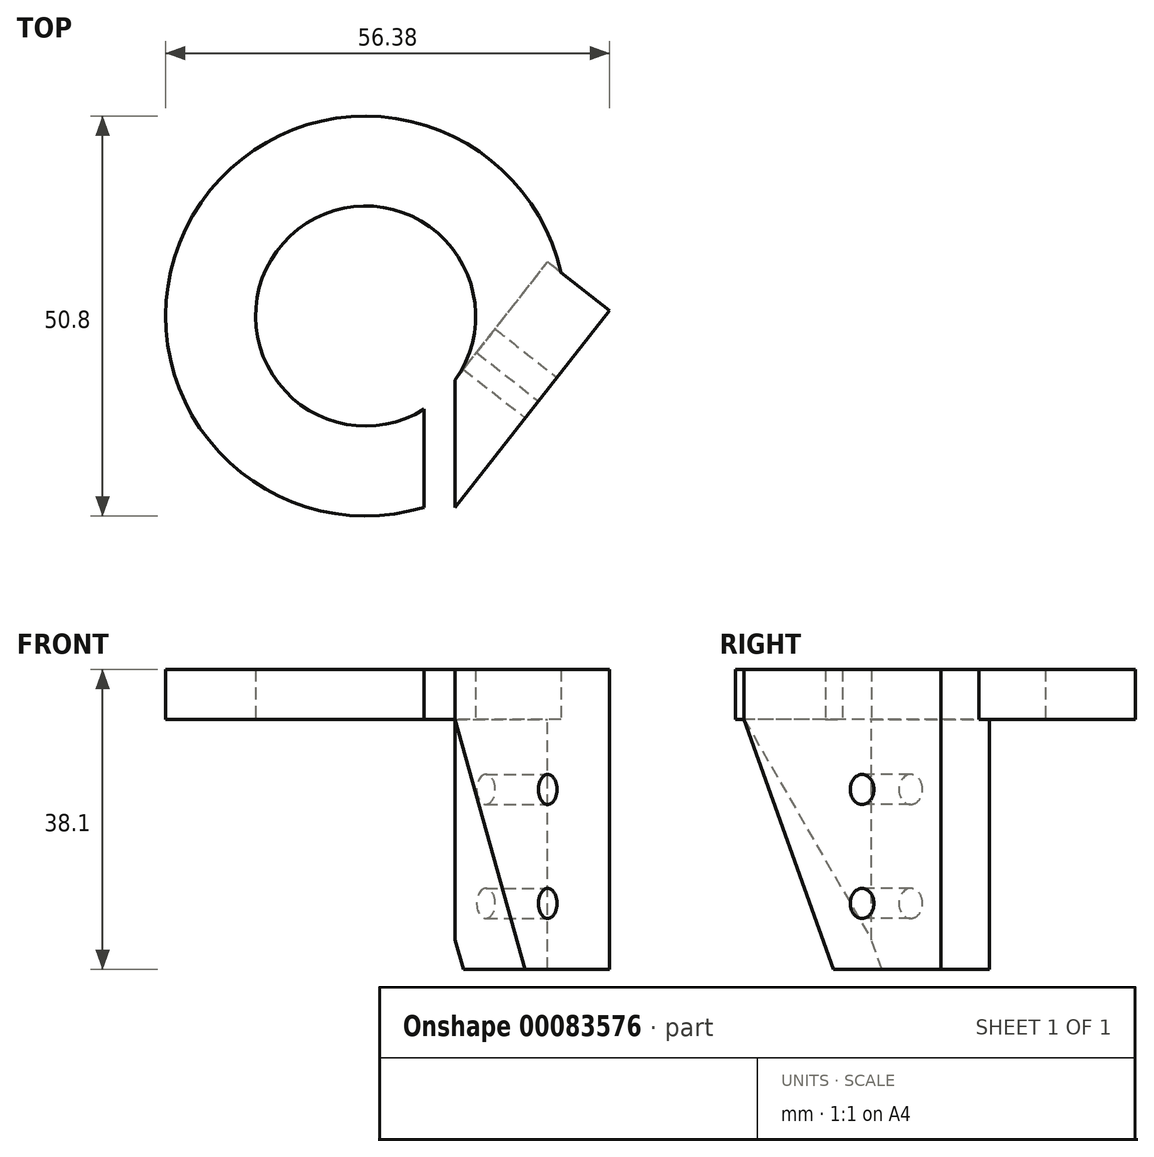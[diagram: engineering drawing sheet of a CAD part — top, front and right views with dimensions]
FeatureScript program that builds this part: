
annotation { "Feature Type Name" : "Feature", "Feature Type Description" : "" }
export const myFeature = defineFeature(function(context is Context, id is Id, definition is map)
    precondition{}
    {
        {
            var Q0;
            Q0=qCreatedBy(makeId("Top.planeOp"),FACE);
            var sketch = newSketch(context, id + "F0", { "sketchPlane" : qUnion([Q0])});
            skLineSegment(sketch, "E0.bottom", {"start": v(0, 0) * mm, "end": v(12.7, 0) * mm});
            skLineSegment(sketch, "E0.left", {"start": v(0, 0) * mm, "end": v(0, 50.8) * mm});
            skLineSegment(sketch, "E0.right", {"start": v(12.7, 0) * mm, "end": v(12.7, 50.8) * mm});
            skArc(sketch, "E1", {"start": v(0, 50.8) * mm, "mid": v(-20.94, 69.1) * mm, "end": v(-3.94, 47.09) * mm});
            skArc(sketch, "E2", {"start": v(12.7, 50.8) * mm, "mid": v(-29.07, 77.14) * mm, "end": v(-3.94, 34.63) * mm});
            skLineSegment(sketch, "E3", {"start": v(-3.94, 47.09) * mm, "end": v(-3.94, 34.63) * mm});
            skSolve(sketch);
        }
        {
            var Q0;
            Q0 = qSketchRegion(id + "F0", true);
            extrude(context, id + "F1", {"entities" : qUnion([Q0]), "depth" : 6.35 * mm});
        }
        {
            var Q0;
            Q0=makeQuery(id+"F1.opExtrude","CAP_FACE",FACE,{"disambiguationData":[OSD([sQuery(id+"F0.wireOp",EDGE,"E0.bottom"),sQuery(id+"F0.wireOp",EDGE,"E0.left"),sQuery(id+"F0.wireOp",EDGE,"E0.right"),sQuery(id+"F0.wireOp",EDGE,"E1"),sQuery(id+"F0.wireOp",EDGE,"E2"),sQuery(id+"F0.wireOp",EDGE,"E3")])],"isStart":true});
            var sketch = newSketch(context, id + "F2", { "sketchPlane" : qUnion([Q0])});
            skLineSegment(sketch, "E4.bottom", {"start": v(19.05, 0) * mm, "end": v(-6.35, 0) * mm});
            skLineSegment(sketch, "E4.top", {"start": v(19.05, -7.62) * mm, "end": v(-6.35, -7.62) * mm});
            skLineSegment(sketch, "E4.left", {"start": v(19.05, 0) * mm, "end": v(19.05, -7.62) * mm});
            skLineSegment(sketch, "E4.right", {"start": v(-6.35, 0) * mm, "end": v(-6.35, -7.62) * mm});
            skSolve(sketch);
        }
        {
            var Q0;
            Q0 = qSketchRegion(id + "F2", true);
            extrude(context, id + "F3", {"entities" : qUnion([Q0]), "operationType" : NewBodyOperationType.ADD, "depth" : 50.8 * mm, "hasSecondDirection" : true, "secondDirectionOppositeDirection" : true, "secondDirectionDepth" : 6.35 * mm});
        }
        {
            var Q0;
            Q0=makeQuery(id+"F3.boolean.opBoolean","MERGE",FACE,{"derivedFrom":[makeQuery(id+"F1.opExtrude","SWEPT_FACE",FACE,{"disambiguationData":[OSD([sQuery(id+"F0.wireOp",EDGE,"E0.bottom")])]}),makeQuery(id+"F3.opExtrude","SWEPT_FACE",FACE,{"disambiguationData":[OSD([sQuery(id+"F2.wireOp",EDGE,"E4.bottom")])]})]});
            var sketch = newSketch(context, id + "F4", { "sketchPlane" : qUnion([Q0])});
            skCircle(sketch, "E5", {"center": v(6.35, -8.89) * mm, "radius": 1.9 * mm});
            skCircle(sketch, "E6", {"center": v(6.35, -23.37) * mm, "radius": 1.9 * mm});
            skSolve(sketch);
        }
        {
            var Q0;
            Q0=makeQuery(id+"F4.imprint","IMPRINT",FACE,{"disambiguationData":[TD([[makeQuery(id+"F4.imprint","IMPRINT",EDGE,{"derivedFrom":sQuery(id+"F4.wireOp",EDGE,"E5")}),1.0]])]});
            var Q1;
            Q1=makeQuery(id+"F4.imprint","IMPRINT",FACE,{"disambiguationData":[TD([[makeQuery(id+"F4.imprint","IMPRINT",EDGE,{"derivedFrom":sQuery(id+"F4.wireOp",EDGE,"E6")}),1.0]])]});
            extrude(context, id + "F5", {"entities" : qUnion([Q0, Q1]), "operationType" : NewBodyOperationType.REMOVE, "oppositeDirection" : true, "depth" : 25.4 * mm});
        }
        {
            var Q0;
            Q0=makeQuery(id+"F3.opExtrude","SWEPT_FACE",FACE,{"disambiguationData":[OSD([sQuery(id+"F2.wireOp",EDGE,"E4.top")])]});
            var sketch = newSketch(context, id + "F6", { "sketchPlane" : qUnion([Q0])});
            skLineSegment(sketch, "E7.bottom", {"start": v(6.35, -50.8) * mm, "end": v(-19.05, -50.8) * mm});
            skLineSegment(sketch, "E7.top", {"start": v(6.35, -38.1) * mm, "end": v(-19.05, -38.1) * mm});
            skLineSegment(sketch, "E7.left", {"start": v(6.35, -50.8) * mm, "end": v(6.35, -38.1) * mm});
            skLineSegment(sketch, "E7.right", {"start": v(-19.05, -50.8) * mm, "end": v(-19.05, -38.1) * mm});
            skSolve(sketch);
        }
        {
            var Q0;
            Q0 = qSketchRegion(id + "F6", true);
            extrude(context, id + "F7", {"entities" : qUnion([Q0]), "operationType" : NewBodyOperationType.REMOVE, "oppositeDirection" : true, "depth" : 25.4 * mm});
        }
        {
            var Q0;
            Q0=makeQuery(id+"F3.boolean.opBoolean","MERGE",FACE,{"derivedFrom":[makeQuery(id+"F1.opExtrude","CAP_FACE",FACE,{"disambiguationData":[OSD([sQuery(id+"F0.wireOp",EDGE,"E0.bottom"),sQuery(id+"F0.wireOp",EDGE,"E0.left"),sQuery(id+"F0.wireOp",EDGE,"E0.right"),sQuery(id+"F0.wireOp",EDGE,"E1"),sQuery(id+"F0.wireOp",EDGE,"E2"),sQuery(id+"F0.wireOp",EDGE,"E3")])],"isStart":false}),makeQuery(id+"F3.opExtrude","CAP_FACE",FACE,{"disambiguationData":[OSD([sQuery(id+"F2.wireOp",EDGE,"E4.bottom"),sQuery(id+"F2.wireOp",EDGE,"E4.top"),sQuery(id+"F2.wireOp",EDGE,"E4.left"),sQuery(id+"F2.wireOp",EDGE,"E4.right")])],"isStart":true})]});
            var sketch = newSketch(context, id + "F8", { "sketchPlane" : qUnion([Q0])});
            skLineSegment(sketch, "E8.left", {"start": v(0, 34.63) * mm, "end": v(0, 17.32) * mm});
            skLineSegment(sketch, "E8.right", {"start": v(37.46, 34.63) * mm, "end": v(37.46, 0) * mm});
            skLineSegment(sketch, "E9", {"start": v(0, 17.32) * mm, "end": v(-24.97, 14.05) * mm});
            skLineSegment(sketch, "E10", {"start": v(-24.97, 14.05) * mm, "end": v(-24.97, -25.6) * mm});
            skLineSegment(sketch, "E11", {"start": v(-24.97, -25.6) * mm, "end": v(41.82, -22.47) * mm});
            skLineSegment(sketch, "E12", {"start": v(41.82, -22.47) * mm, "end": v(37.46, 0) * mm});
            skPoint(sketch, "E13.orphan", {"position": v(0, 0) * mm});
            skLineSegment(sketch, "E14", {"start": v(0, 34.63) * mm, "end": v(12.7, 50.8) * mm});
            skLineSegment(sketch, "E15", {"start": v(12.7, 50.8) * mm, "end": v(37.46, 34.63) * mm});
            skSolve(sketch);
        }
        {
            var Q0;
            Q0 = qSketchRegion(id + "F8", true);
            extrude(context, id + "F9", {"entities" : qUnion([Q0]), "operationType" : NewBodyOperationType.REMOVE, "oppositeDirection" : true, "depth" : 50.8 * mm});
        }
        {
            var Q0;
            Q0=makeQuery(id+"F3.boolean.opBoolean","MERGE",FACE,{"derivedFrom":[makeQuery(id+"F1.opExtrude","CAP_FACE",FACE,{"disambiguationData":[OSD([sQuery(id+"F0.wireOp",EDGE,"E0.bottom"),sQuery(id+"F0.wireOp",EDGE,"E0.left"),sQuery(id+"F0.wireOp",EDGE,"E0.right"),sQuery(id+"F0.wireOp",EDGE,"E1"),sQuery(id+"F0.wireOp",EDGE,"E2"),sQuery(id+"F0.wireOp",EDGE,"E3")])],"isStart":false}),makeQuery(id+"F3.opExtrude","CAP_FACE",FACE,{"disambiguationData":[OSD([sQuery(id+"F2.wireOp",EDGE,"E4.bottom"),sQuery(id+"F2.wireOp",EDGE,"E4.top"),sQuery(id+"F2.wireOp",EDGE,"E4.left"),sQuery(id+"F2.wireOp",EDGE,"E4.right")])],"isStart":true})]});
            var sketch = newSketch(context, id + "F10", { "sketchPlane" : qUnion([Q0])});
            skLineSegment(sketch, "E16", {"start": v(0, 34.63) * mm, "end": v(0, 50.8) * mm});
            skLineSegment(sketch, "E17", {"start": v(0, 50.8) * mm, "end": v(11.76, 65.77) * mm});
            skLineSegment(sketch, "E18", {"start": v(0, 34.63) * mm, "end": v(19.61, 59.6) * mm});
            skLineSegment(sketch, "E19", {"start": v(19.61, 59.6) * mm, "end": v(11.76, 65.77) * mm});
            skSolve(sketch);
        }
        {
            var Q0;
            Q0 = qSketchRegion(id + "F10", true);
            extrude(context, id + "F11", {"entities" : qUnion([Q0]), "operationType" : NewBodyOperationType.ADD, "oppositeDirection" : true, "depth" : 38.1 * mm});
        }
        {
            var Q0;
            Q0=makeQuery(id+"F11.boolean.opBoolean","MERGE",FACE,{"derivedFrom":[makeQuery(id+"F9.boolean.opBoolean","COPY",FACE,{"derivedFrom":makeQuery(id+"F9.opExtrude","SWEPT_FACE",FACE,{"disambiguationData":[OSD([sQuery(id+"F8.wireOp",EDGE,"E14")])]})}),makeQuery(id+"F11.opExtrude","SWEPT_FACE",FACE,{"disambiguationData":[OSD([sQuery(id+"F10.wireOp",EDGE,"E18")])]})]});
            var sketch = newSketch(context, id + "F12", { "sketchPlane" : qUnion([Q0])});
            skCircle(sketch, "E20", {"center": v(46.28, -8.89) * mm, "radius": 1.9 * mm});
            skCircle(sketch, "E21", {"center": v(46.28, -23.37) * mm, "radius": 1.9 * mm});
            skSolve(sketch);
        }
        {
            var Q0;
            Q0 = qSketchRegion(id + "F12", true);
            extrude(context, id + "F13", {"entities" : qUnion([Q0]), "operationType" : NewBodyOperationType.REMOVE, "oppositeDirection" : true, "depth" : 25.4 * mm});
        }
        {
            var Q0;
            Q0=makeQuery(id+"F11.boolean.opBoolean","MERGE",FACE,{"derivedFrom":[makeQuery(id+"F9.boolean.opBoolean","COPY",FACE,{"derivedFrom":makeQuery(id+"F9.opExtrude","SWEPT_FACE",FACE,{"disambiguationData":[OSD([sQuery(id+"F8.wireOp",EDGE,"E14")])]})}),makeQuery(id+"F11.opExtrude","SWEPT_FACE",FACE,{"disambiguationData":[OSD([sQuery(id+"F10.wireOp",EDGE,"E18")])]})]});
            var sketch = newSketch(context, id + "F14", { "sketchPlane" : qUnion([Q0])});
            skLineSegment(sketch, "E22", {"start": v(41.66, -31.75) * mm, "end": v(27.23, 0) * mm});
            skLineSegment(sketch, "E23", {"start": v(27.23, 0) * mm, "end": v(27.23, -31.75) * mm});
            skLineSegment(sketch, "E24", {"start": v(27.23, -31.75) * mm, "end": v(41.66, -31.75) * mm});
            skSolve(sketch);
        }
        {
            var Q0;
            Q0 = qSketchRegion(id + "F14", true);
            extrude(context, id + "F15", {"entities" : qUnion([Q0]), "operationType" : NewBodyOperationType.REMOVE, "oppositeDirection" : true, "depth" : 25.4 * mm});
        }
    });
